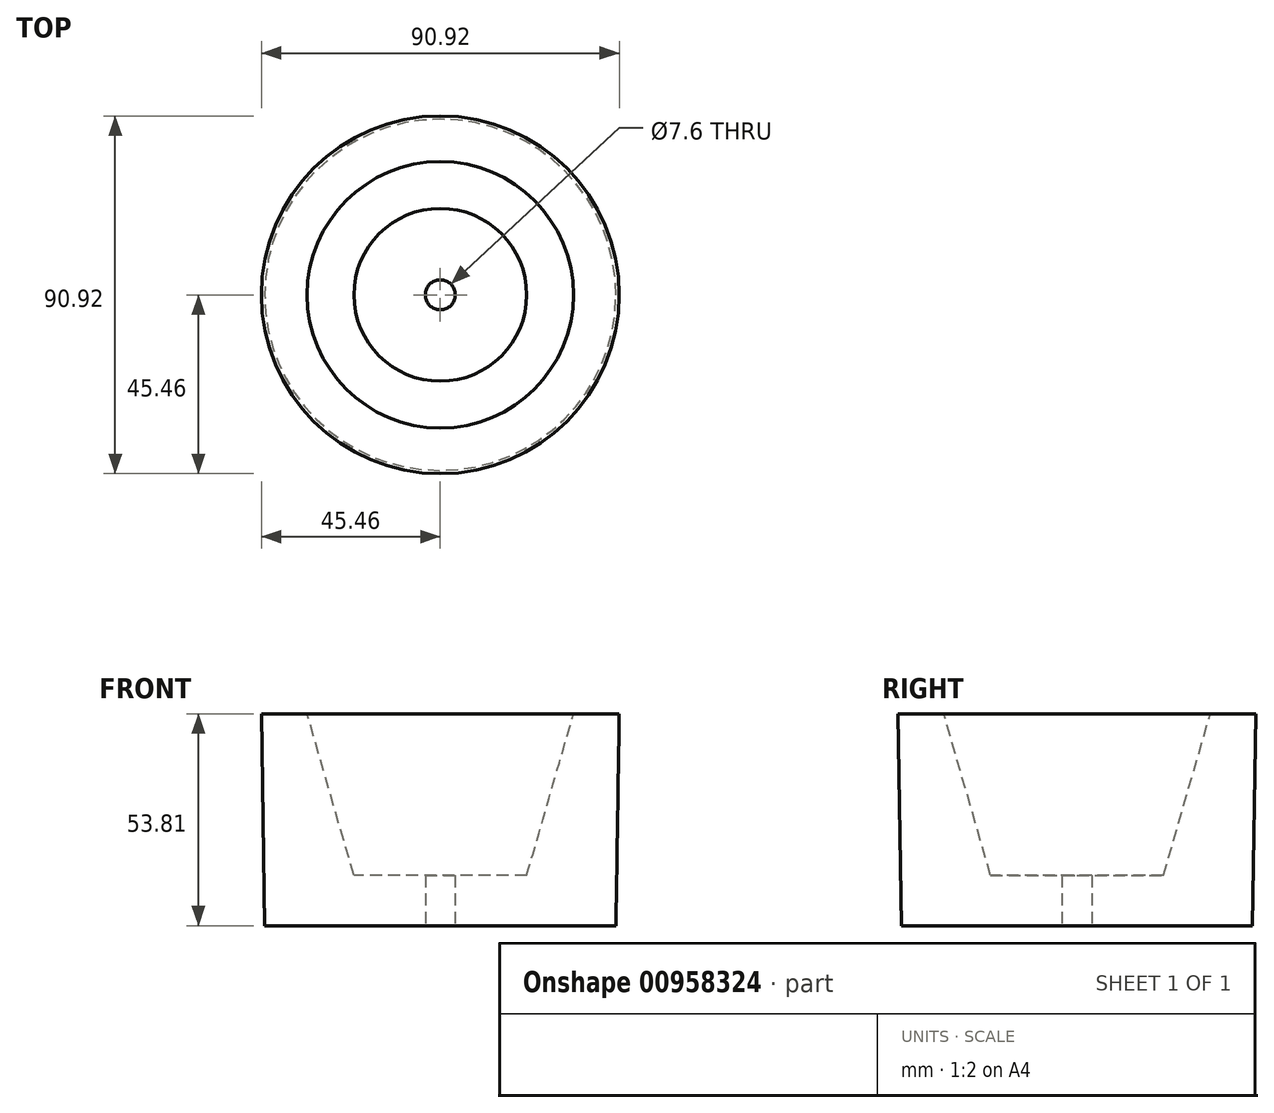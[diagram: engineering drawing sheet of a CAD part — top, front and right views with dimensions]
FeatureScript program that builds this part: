
annotation { "Feature Type Name" : "Feature", "Feature Type Description" : "" }
export const myFeature = defineFeature(function(context is Context, id is Id, definition is map)
    precondition{}
    {
        {
            var Q0;
            Q0=qCreatedBy(makeId("Front.planeOp"),FACE);
            var sketch = newSketch(context, id + "F0", { "sketchPlane" : qUnion([Q0])});
            skLineSegment(sketch, "E0", {"start": v(-45.46, 29.74) * mm, "end": v(-33.84, 29.74) * mm});
            skLineSegment(sketch, "E1", {"start": v(-33.84, 29.74) * mm, "end": v(-21.95, -11.33) * mm});
            skLineSegment(sketch, "E2", {"start": v(-21.95, -11.33) * mm, "end": v(0, -11.33) * mm});
            skLineSegment(sketch, "E3", {"start": v(0, -11.33) * mm, "end": v(0, -24.07) * mm});
            skLineSegment(sketch, "E4", {"start": v(0, -24.07) * mm, "end": v(-44.6, -24.07) * mm});
            skLineSegment(sketch, "E5", {"start": v(-44.6, -24.07) * mm, "end": v(-45.46, 29.74) * mm});
            skLineSegment(sketch, "E6", {"start": v(0, 43.9) * mm, "end": v(0, -49.28) * mm, "construction": true});
            skSolve(sketch);
        }
        {
            var Q0;
            Q0=makeQuery(id+"F0.imprint","IMPRINT",FACE,{"disambiguationData":[TD([[makeQuery(id+"F0.imprint","IMPRINT",EDGE,{"derivedFrom":sQuery(id+"F0.wireOp",EDGE,"E0")}),-1.0]])]});
            var Q1;
            Q1=sQuery(id+"F0.wireOp",EDGE,"E6");
            revolve(context, id + "F1", {"surfaceOperationType" : NewSurfaceOperationType.NEW, "entities" : qUnion([Q0]), "axis" : qUnion([Q1]), "revolveType" : RevolveType.FULL});
        }
        {
            var Q0;
            Q0=makeQuery(id+"F1.opRevolve","SWEPT_FACE",FACE,{"disambiguationData":[OSD([sQuery(id+"F0.wireOp",EDGE,"E4")])]});
            var sketch = newSketch(context, id + "F2", { "sketchPlane" : qUnion([Q0])});
            skPoint(sketch, "E7", {"position": v(0, 0) * mm});
            skPoint(sketch, "E8", {"position": v(0.7, 0) * mm});
            skSolve(sketch);
        }
        {
            var Q0;
            Q0=sQuery(id+"F2.wireOp",VERTEX,"E7");
            var Q1;
            Q1=makeQuery(id+"FxU4RIqOX824l7G_1.opExtrude","SWEPT_BODY",BODY,{"disambiguationData":[OSD([sQuery(id+"FGKrHFZuWE7Ya2d_1.wireOp",EDGE,"I9WXwtrn-dc41-gXbk-6oa6-y5aQgftULHsy")])]});
            var Q2;
            Q2=makeQuery(id+"F1.opRevolve","SWEPT_BODY",BODY,{"disambiguationData":[OSD([sQuery(id+"F0.wireOp",EDGE,"E0"),sQuery(id+"F0.wireOp",EDGE,"E1"),sQuery(id+"F0.wireOp",EDGE,"E2"),sQuery(id+"F0.wireOp",EDGE,"E3"),sQuery(id+"F0.wireOp",EDGE,"E4"),sQuery(id+"F0.wireOp",EDGE,"E5")])]});
            hole(context, id + "F3", {"style" : HoleStyle.SIMPLE, "endStyle" : HoleEndStyle.THROUGH, "standardTappedOrClearance" : lookupTablePath({ "fit" : "Normal", "standard" : "ISO", "size" : "M7", "type" : "Clearance" }), "standardBlindInLast" : lookupTablePath({ "fit" : "Normal", "standard" : "ISO", "engagement" : "75%", "pitch" : "0.75 mm", "size" : "M7", "type" : "Clearance & tapped" }), "holeDiameter" : 7.6 * mm, "majorDiameter" : 6.35 * mm, "isTappedThrough" : true, "tappedDepth" : 12.7 * mm, "tapClearance" : 3, "locations" : qUnion([Q0]), "scope" : qUnion([Q1, Q2])});
        }
    });
